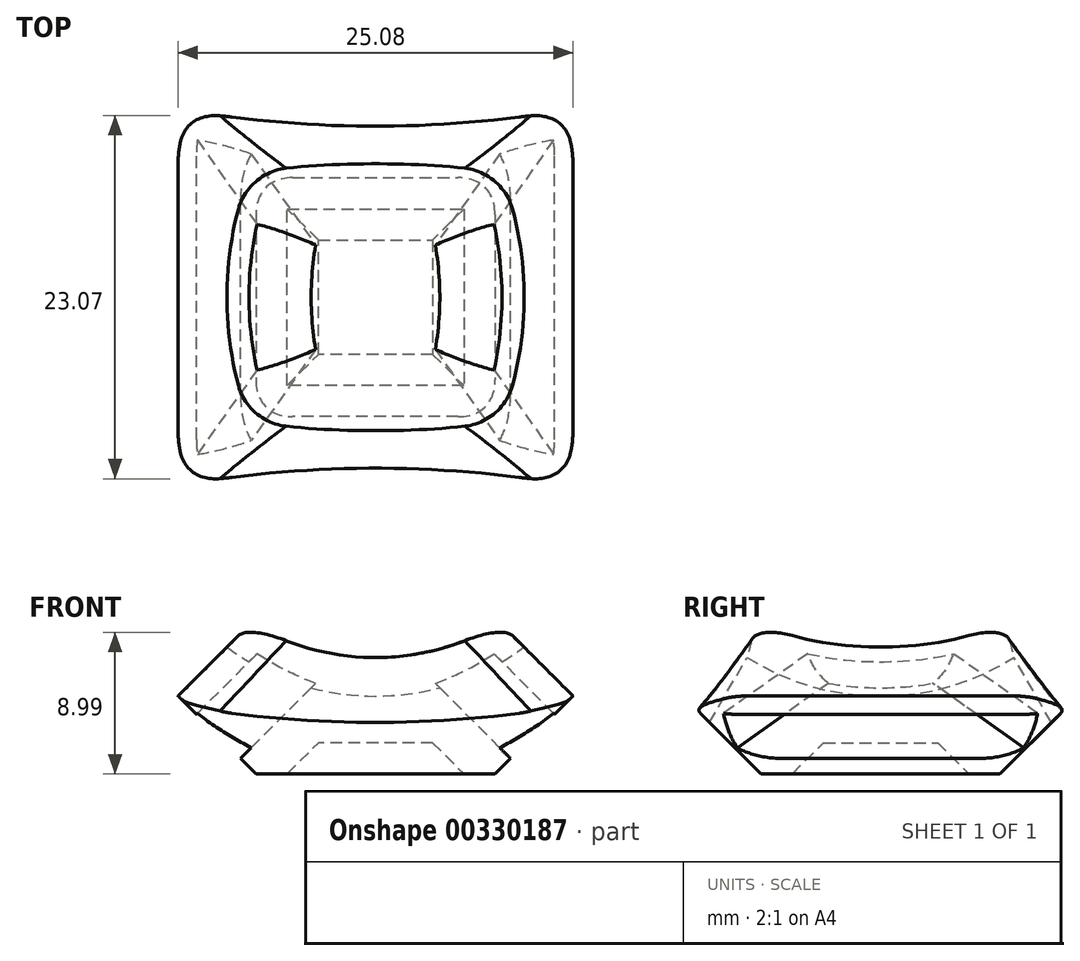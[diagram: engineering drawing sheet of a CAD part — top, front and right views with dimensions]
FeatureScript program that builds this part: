
annotation { "Feature Type Name" : "Feature", "Feature Type Description" : "" }
export const myFeature = defineFeature(function(context is Context, id is Id, definition is map)
    precondition{}
    {
        {
            var Q0;
            Q0=qCreatedBy(makeId("Top.planeOp"),FACE);
            var sketch = newSketch(context, id + "F0", { "sketchPlane" : qUnion([Q0])});
            skLineSegment(sketch, "E0.bottom", {"start": v(-12.43, 22.7) * mm, "end": v(7.57, 22.7) * mm});
            skLineSegment(sketch, "E0.top", {"start": v(-12.43, -17.3) * mm, "end": v(7.57, -17.3) * mm});
            skLineSegment(sketch, "E0.left", {"start": v(-12.43, 22.7) * mm, "end": v(-12.43, -17.3) * mm});
            skLineSegment(sketch, "E0.right", {"start": v(7.57, 22.7) * mm, "end": v(7.57, -17.3) * mm});
            skSolve(sketch);
        }
        {
            var Q0;
            Q0=qSketchRegion(id+"F0",true);
            extrude(context, id + "F1", {"entities" : qUnion([Q0]), "depth" : 20 * mm});
        }
        {
            var Q0;
            Q0=makeQuery(id+"F1.opExtrude","CAP_EDGE",EDGE,{"disambiguationData":[OSD([sQuery(id+"F0.wireOp",EDGE,"E0.right")])],"isStart":false});
            var Q1;
            Q1=makeQuery(id+"F1.opExtrude","CAP_EDGE",EDGE,{"disambiguationData":[OSD([sQuery(id+"F0.wireOp",EDGE,"E0.top")])],"isStart":false});
            var Q2;
            Q2=makeQuery(id+"F1.opExtrude","CAP_EDGE",EDGE,{"disambiguationData":[OSD([sQuery(id+"F0.wireOp",EDGE,"E0.bottom")])],"isStart":false});
            chamfer(context, id + "F2", {"entities" : qUnion([Q0, Q1, Q2]), "width" : 20 * mm, "tangentPropagation" : true});
        }
        {
            var Q0;
            Q0=makeQuery(id+"F1.opExtrude","CAP_FACE",FACE,{"disambiguationData":[OSD([sQuery(id+"F0.wireOp",EDGE,"E0.bottom"),sQuery(id+"F0.wireOp",EDGE,"E0.top"),sQuery(id+"F0.wireOp",EDGE,"E0.left"),sQuery(id+"F0.wireOp",EDGE,"E0.right")])],"isStart":true});
            extrude(context, id + "F3", {"entities" : qUnion([Q0]), "operationType" : NewBodyOperationType.ADD, "depth" : 6.5 * mm});
        }
        {
            var Q0;
            {var subQ0=sQuery(id+"F0.wireOp",EDGE,"E0.right");var subQ1=sQuery(id+"F0.wireOp",EDGE,"E0.left");var subQ2=sQuery(id+"F0.wireOp",EDGE,"E0.top");var subQ3=sQuery(id+"F0.wireOp",EDGE,"E0.bottom");Q0=makeQuery(id+"F3.opExtrude","CAP_EDGE",EDGE,{"disambiguationData":[OSD([subQ3,subQ2,subQ1,subQ0]),TDD([makeQuery(id+"F2.opChamfer","BLEND_EDGE",EDGE,{"blendedFrom":[makeQuery(id+"F1.opExtrude","CAP_EDGE",EDGE,{"disambiguationData":[OSD([subQ0])],"isStart":false}),makeQuery(id+"F1.opExtrude","CAP_FACE",FACE,{"disambiguationData":[OSD([subQ3,subQ2,subQ1,subQ0])],"isStart":true})],"blendedInto":[makeQuery(id+"F1.opExtrude","CAP_FACE",FACE,{"disambiguationData":[OSD([subQ3,subQ2,subQ1,subQ0])],"isStart":true})]})])],"isStart":false});}
            var Q1;
            {var subQ0=sQuery(id+"F0.wireOp",EDGE,"E0.right");var subQ1=sQuery(id+"F0.wireOp",EDGE,"E0.left");var subQ2=sQuery(id+"F0.wireOp",EDGE,"E0.top");var subQ3=sQuery(id+"F0.wireOp",EDGE,"E0.bottom");Q1=makeQuery(id+"F3.opExtrude","CAP_EDGE",EDGE,{"disambiguationData":[OSD([subQ3,subQ2,subQ1,subQ0]),TDD([makeQuery(id+"F2.opChamfer","BLEND_EDGE",EDGE,{"blendedFrom":[makeQuery(id+"F1.opExtrude","CAP_EDGE",EDGE,{"disambiguationData":[OSD([subQ3])],"isStart":false}),makeQuery(id+"F1.opExtrude","CAP_FACE",FACE,{"disambiguationData":[OSD([subQ3,subQ2,subQ1,subQ0])],"isStart":true})],"blendedInto":[makeQuery(id+"F1.opExtrude","CAP_FACE",FACE,{"disambiguationData":[OSD([subQ3,subQ2,subQ1,subQ0])],"isStart":true})]})])],"isStart":false});}
            var Q2;
            {var subQ0=sQuery(id+"F0.wireOp",EDGE,"E0.right");var subQ1=sQuery(id+"F0.wireOp",EDGE,"E0.left");var subQ2=sQuery(id+"F0.wireOp",EDGE,"E0.top");var subQ3=sQuery(id+"F0.wireOp",EDGE,"E0.bottom");Q2=makeQuery(id+"F3.opExtrude","CAP_EDGE",EDGE,{"disambiguationData":[OSD([subQ3,subQ2,subQ1,subQ0]),TDD([makeQuery(id+"F2.opChamfer","BLEND_EDGE",EDGE,{"blendedFrom":[makeQuery(id+"F1.opExtrude","CAP_EDGE",EDGE,{"disambiguationData":[OSD([subQ2])],"isStart":false}),makeQuery(id+"F1.opExtrude","CAP_FACE",FACE,{"disambiguationData":[OSD([subQ3,subQ2,subQ1,subQ0])],"isStart":true})],"blendedInto":[makeQuery(id+"F1.opExtrude","CAP_FACE",FACE,{"disambiguationData":[OSD([subQ3,subQ2,subQ1,subQ0])],"isStart":true})]})])],"isStart":false});}
            chamfer(context, id + "F4", {"entities" : qUnion([Q0, Q1, Q2]), "chamferType" : ChamferType.OFFSET_ANGLE, "width" : 8.5 * mm, "oppositeDirection" : false, "angle" : 45 * degree, "tangentPropagation" : true});
        }
        {
            var Q0;
            Q0=makeQuery(id+"F2.opChamfer","BLEND_FACE",FACE,{"disambiguationData":[OSD([sQuery(id+"F0.wireOp",EDGE,"E0.right")])]});
            cPlane(context, id + "F5", {"entities" : qUnion([Q0]), "cplaneType" : CPlaneType.OFFSET, "offset" : 5.5 * mm, "oppositeDirection" : true, "width" : 150 * mm, "height" : 150 * mm});
        }
        {
            var Q0;
            Q0=qCreatedBy(id+"F5.planeOp",FACE);
            var sketch = newSketch(context, id + "F6", { "sketchPlane" : qUnion([Q0])});
            skLineSegment(sketch, "E1", {"start": v(2.7, 11.3) * mm, "end": v(-12.55, -3.94) * mm});
            skLineSegment(sketch, "E2", {"start": v(-12.55, -3.94) * mm, "end": v(17.95, -3.94) * mm});
            skLineSegment(sketch, "E3", {"start": v(17.95, -3.94) * mm, "end": v(2.7, 11.3) * mm});
            skSolve(sketch);
        }
        {
            var Q0;
            Q0=qSketchRegion(id+"F6",true);
            extrude(context, id + "F7", {"entities" : qUnion([Q0]), "operationType" : NewBodyOperationType.REMOVE, "oppositeDirection" : true, "depth" : 6 * mm, "symmetric" : true});
        }
        {
            var Q0;
            Q0=makeQuery(id+"F1.opExtrude","SWEPT_BODY",BODY,{"disambiguationData":[OSD([sQuery(id+"F0.wireOp",EDGE,"E0.bottom"),sQuery(id+"F0.wireOp",EDGE,"E0.top"),sQuery(id+"F0.wireOp",EDGE,"E0.left"),sQuery(id+"F0.wireOp",EDGE,"E0.right")])]});
            var Q1;
            {var subQ0=sQuery(id+"F0.wireOp",EDGE,"E0.left");Q1=makeQuery(id+"F3.boolean.opBoolean","MERGE",FACE,{"derivedFrom":[makeQuery(id+"F1.opExtrude","SWEPT_FACE",FACE,{"disambiguationData":[OSD([subQ0])]}),makeQuery(id+"F3.opExtrude","SWEPT_FACE",FACE,{"disambiguationData":[OSD([subQ0])]})]});}
            mirror(context, id + "F8", {"operationType" : NewBodyOperationType.ADD, "entities" : qUnion([Q0]), "mirrorPlane" : qUnion([Q1])});
        }
        {
            var Q0;
            Q0=qCreatedBy(makeId("Top.planeOp"),FACE);
            cPlane(context, id + "F9", {"entities" : qUnion([Q0]), "cplaneType" : CPlaneType.OFFSET, "offset" : 25 * mm, "width" : 150 * mm, "height" : 150 * mm});
        }
        {
            var Q0;
            Q0=qCreatedBy(id+"F9.planeOp",FACE);
            var sketch = newSketch(context, id + "F10", { "sketchPlane" : qUnion([Q0])});
            skArc(sketch, "E4", {"start": v(-12.43, 26.72) * mm, "mid": v(-36.44, 2.7) * mm, "end": v(-12.43, -21.32) * mm});
            skLineSegment(sketch, "E5", {"start": v(-12.43, 40.8) * mm, "end": v(-12.43, -65.38) * mm, "construction": true});
            skLineSegment(sketch, "E6", {"start": v(-12.43, 26.72) * mm, "end": v(-12.43, -21.32) * mm});
            skSolve(sketch);
        }
        {
            var Q0;
            Q0=qCreatedBy(id+"F9.planeOp",FACE);
            cPlane(context, id + "F11", {"entities" : qUnion([Q0]), "cplaneType" : CPlaneType.OFFSET, "offset" : 41.1 * mm, "oppositeDirection" : true, "width" : 150 * mm, "height" : 150 * mm});
        }
        {
            var Q0;
            Q0=qSketchRegion(id+"F10",true);
            var Q1;
            Q1=sQuery(id+"F10.wireOp",EDGE,"E5");
            revolve(context, id + "F12", {"operationType" : NewBodyOperationType.REMOVE, "entities" : qUnion([Q0]), "axis" : qUnion([Q1]), "revolveType" : RevolveType.FULL, "oppositeDirection" : true});
        }
        {
            var Q0;
            Q0=qCreatedBy(id+"F11.planeOp",FACE);
            var sketch = newSketch(context, id + "F13", { "sketchPlane" : qUnion([Q0])});
            skCircle(sketch, "E7", {"center": v(-12.43, 87.55) * mm, "radius": 60 * mm});
            skCircle(sketch, "E8", {"center": v(-12.43, -82.15) * mm, "radius": 60 * mm});
            skLineSegment(sketch, "E9", {"start": v(-12.43, 87.55) * mm, "end": v(-12.43, -82.15) * mm, "construction": true});
            skSolve(sketch);
        }
        {
            var Q0;
            Q0=makeQuery(id+"F13.imprint","IMPRINT",FACE,{"disambiguationData":[TD([[makeQuery(id+"F13.imprint","IMPRINT",EDGE,{"derivedFrom":sQuery(id+"F13.wireOp",EDGE,"E7")}),1.0]])]});
            var Q1;
            Q1=makeQuery(id+"F13.imprint","IMPRINT",FACE,{"disambiguationData":[TD([[makeQuery(id+"F13.imprint","IMPRINT",EDGE,{"derivedFrom":sQuery(id+"F13.wireOp",EDGE,"E8")}),1.0]])]});
            extrude(context, id + "F14", {"entities" : qUnion([Q0, Q1]), "operationType" : NewBodyOperationType.REMOVE, "depth" : 33.1 * mm, "hasDraft" : true, "draftAngle" : 30 * degree});
        }
        {
            var Q0;
            {var subQ0=makeQuery(id+"F3.opExtrude","CAP_FACE",FACE,{"disambiguationData":[OSD([sQuery(id+"F0.wireOp",EDGE,"E0.bottom"),sQuery(id+"F0.wireOp",EDGE,"E0.top"),sQuery(id+"F0.wireOp",EDGE,"E0.left"),sQuery(id+"F0.wireOp",EDGE,"E0.right")])],"isStart":false});Q0=makeQuery(id+"F8.boolean.opBoolean","MERGE",FACE,{"derivedFrom":[subQ0,makeQuery(id+"F8.opPattern","COPY",FACE,{"derivedFrom":subQ0,"instanceName":"1"})]});}
            var sketch = newSketch(context, id + "F15", { "sketchPlane" : qUnion([Q0])});
            skLineSegment(sketch, "E10.bottom", {"start": v(-20.93, 5.8) * mm, "end": v(-3.93, 5.8) * mm});
            skLineSegment(sketch, "E10.top", {"start": v(-20.93, -11.2) * mm, "end": v(-3.93, -11.2) * mm});
            skLineSegment(sketch, "E10.left", {"start": v(-20.93, 5.8) * mm, "end": v(-20.93, -11.2) * mm});
            skLineSegment(sketch, "E10.right", {"start": v(-3.93, 5.8) * mm, "end": v(-3.93, -11.2) * mm});
            skPoint(sketch, "E10.middle", {"position": v(-12.43, -2.7) * mm});
            skPoint(sketch, "E10.middle.positionSnap0", {"position": v(-23.93, -2.7) * mm});
            skPoint(sketch, "E10.middle.positionSnap1", {"position": v(-12.43, 8.8) * mm});
            skPoint(sketch, "E10.centerSnap0", {"position": v(-23.93, -2.7) * mm});
            skPoint(sketch, "E10.centerSnap1", {"position": v(-12.43, 8.8) * mm});
            skSolve(sketch);
        }
        {
            var Q0;
            Q0 = qSketchRegion(id + "F15", true);
            extrude(context, id + "F16", {"entities" : qUnion([Q0]), "operationType" : NewBodyOperationType.REMOVE, "oppositeDirection" : true, "depth" : 3 * mm, "hasDraft" : true, "draftAngle" : 45 * degree, "draftPullDirection" : true});
        }
        {
            var Q0;
            Q0=makeQuery(id+"F14.boolean.opBoolean","INTERSECT",EDGE,{"derivedFrom":[makeQuery(id+"F2.opChamfer","BLEND_FACE",FACE,{"disambiguationData":[OSD([sQuery(id+"F0.wireOp",EDGE,"E0.right")])]}),makeQuery(id+"F14.opExtrude","SWEPT_FACE",FACE,{"disambiguationData":[OSD([sQuery(id+"F13.wireOp",EDGE,"E7")])]})]});
            var Q1;
            Q1=makeQuery(id+"F14.boolean.opBoolean","INTERSECT",EDGE,{"derivedFrom":[makeQuery(id+"F2.opChamfer","BLEND_FACE",FACE,{"disambiguationData":[OSD([sQuery(id+"F0.wireOp",EDGE,"E0.right")])]}),makeQuery(id+"F14.opExtrude","SWEPT_FACE",FACE,{"disambiguationData":[OSD([sQuery(id+"F13.wireOp",EDGE,"E8")])]})]});
            var Q2;
            Q2=makeQuery(id+"F14.boolean.opBoolean","INTERSECT",EDGE,{"derivedFrom":[makeQuery(id+"F8.opPattern","COPY",FACE,{"derivedFrom":makeQuery(id+"F2.opChamfer","BLEND_FACE",FACE,{"disambiguationData":[OSD([sQuery(id+"F0.wireOp",EDGE,"E0.right")])]}),"instanceName":"1"}),makeQuery(id+"F14.opExtrude","SWEPT_FACE",FACE,{"disambiguationData":[OSD([sQuery(id+"F13.wireOp",EDGE,"E8")])]})]});
            var Q3;
            Q3=makeQuery(id+"F14.boolean.opBoolean","INTERSECT",EDGE,{"derivedFrom":[makeQuery(id+"F8.opPattern","COPY",FACE,{"derivedFrom":makeQuery(id+"F2.opChamfer","BLEND_FACE",FACE,{"disambiguationData":[OSD([sQuery(id+"F0.wireOp",EDGE,"E0.right")])]}),"instanceName":"1"}),makeQuery(id+"F14.opExtrude","SWEPT_FACE",FACE,{"disambiguationData":[OSD([sQuery(id+"F13.wireOp",EDGE,"E7")])]})]});
            fillet(context, id + "F17", {"entities" : qUnion([Q0, Q1, Q2, Q3]), "radius" : 5 * mm, "tangentPropagation" : true, "allowEdgeOverflow" : false});
        }
        {
            var Q0;
            {var subQ0=sQuery(id+"F0.wireOp",EDGE,"E0.right");var subQ1=sQuery(id+"F0.wireOp",EDGE,"E0.left");var subQ2=sQuery(id+"F0.wireOp",EDGE,"E0.top");var subQ3=sQuery(id+"F0.wireOp",EDGE,"E0.bottom");var subQ4=makeQuery(id+"F1.opExtrude","CAP_FACE",FACE,{"disambiguationData":[OSD([subQ3,subQ2,subQ1,subQ0])],"isStart":true});var subQ5=makeQuery(id+"F3.opExtrude","CAP_EDGE",EDGE,{"disambiguationData":[OSD([subQ3,subQ2,subQ1,subQ0]),TDD([makeQuery(id+"F2.opChamfer","BLEND_EDGE",EDGE,{"blendedFrom":[makeQuery(id+"F1.opExtrude","CAP_EDGE",EDGE,{"disambiguationData":[OSD([subQ0])],"isStart":false}),subQ4],"blendedInto":[subQ4]})])],"isStart":false});var subQ6=makeQuery(id+"F3.opExtrude","CAP_EDGE",EDGE,{"disambiguationData":[OSD([subQ3,subQ2,subQ1,subQ0]),TDD([makeQuery(id+"F2.opChamfer","BLEND_EDGE",EDGE,{"blendedFrom":[makeQuery(id+"F1.opExtrude","CAP_EDGE",EDGE,{"disambiguationData":[OSD([subQ2])],"isStart":false}),subQ4],"blendedInto":[subQ4]})])],"isStart":false});Q0=makeQuery(id+"F7.boolean.opBoolean","SPLIT",EDGE,{"disambiguationData":[TD([makeQuery(id+"F2.opChamfer","BLEND_FACE",FACE,{"disambiguationData":[OSD([subQ2])]})])],"derivedFrom":makeQuery(id+"F4.opChamfer","BLEND_EDGE",EDGE,{"blendedFrom":[subQ6,subQ5],"blendedInto":[]})});}
            var Q1;
            {var subQ0=sQuery(id+"F0.wireOp",EDGE,"E0.right");var subQ1=sQuery(id+"F0.wireOp",EDGE,"E0.left");var subQ2=sQuery(id+"F0.wireOp",EDGE,"E0.top");var subQ3=sQuery(id+"F0.wireOp",EDGE,"E0.bottom");var subQ4=makeQuery(id+"F1.opExtrude","CAP_FACE",FACE,{"disambiguationData":[OSD([subQ3,subQ2,subQ1,subQ0])],"isStart":true});var subQ5=makeQuery(id+"F3.opExtrude","CAP_EDGE",EDGE,{"disambiguationData":[OSD([subQ3,subQ2,subQ1,subQ0]),TDD([makeQuery(id+"F2.opChamfer","BLEND_EDGE",EDGE,{"blendedFrom":[makeQuery(id+"F1.opExtrude","CAP_EDGE",EDGE,{"disambiguationData":[OSD([subQ0])],"isStart":false}),subQ4],"blendedInto":[subQ4]})])],"isStart":false});var subQ6=makeQuery(id+"F3.opExtrude","CAP_EDGE",EDGE,{"disambiguationData":[OSD([subQ3,subQ2,subQ1,subQ0]),TDD([makeQuery(id+"F2.opChamfer","BLEND_EDGE",EDGE,{"blendedFrom":[makeQuery(id+"F1.opExtrude","CAP_EDGE",EDGE,{"disambiguationData":[OSD([subQ2])],"isStart":false}),subQ4],"blendedInto":[subQ4]})])],"isStart":false});Q1=makeQuery(id+"F8.opPattern","COPY",EDGE,{"derivedFrom":makeQuery(id+"F7.boolean.opBoolean","SPLIT",EDGE,{"disambiguationData":[TD([makeQuery(id+"F2.opChamfer","BLEND_FACE",FACE,{"disambiguationData":[OSD([subQ2])]})])],"derivedFrom":makeQuery(id+"F4.opChamfer","BLEND_EDGE",EDGE,{"blendedFrom":[subQ6,subQ5],"blendedInto":[]})}),"instanceName":"1"});}
            var Q2;
            {var subQ0=sQuery(id+"F0.wireOp",EDGE,"E0.right");var subQ1=sQuery(id+"F0.wireOp",EDGE,"E0.left");var subQ2=sQuery(id+"F0.wireOp",EDGE,"E0.top");var subQ3=sQuery(id+"F0.wireOp",EDGE,"E0.bottom");var subQ4=makeQuery(id+"F1.opExtrude","CAP_FACE",FACE,{"disambiguationData":[OSD([subQ3,subQ2,subQ1,subQ0])],"isStart":true});var subQ5=makeQuery(id+"F3.opExtrude","CAP_EDGE",EDGE,{"disambiguationData":[OSD([subQ3,subQ2,subQ1,subQ0]),TDD([makeQuery(id+"F2.opChamfer","BLEND_EDGE",EDGE,{"blendedFrom":[makeQuery(id+"F1.opExtrude","CAP_EDGE",EDGE,{"disambiguationData":[OSD([subQ3])],"isStart":false}),subQ4],"blendedInto":[subQ4]})])],"isStart":false});var subQ6=makeQuery(id+"F3.opExtrude","CAP_EDGE",EDGE,{"disambiguationData":[OSD([subQ3,subQ2,subQ1,subQ0]),TDD([makeQuery(id+"F2.opChamfer","BLEND_EDGE",EDGE,{"blendedFrom":[makeQuery(id+"F1.opExtrude","CAP_EDGE",EDGE,{"disambiguationData":[OSD([subQ0])],"isStart":false}),subQ4],"blendedInto":[subQ4]})])],"isStart":false});Q2=makeQuery(id+"F8.opPattern","COPY",EDGE,{"derivedFrom":makeQuery(id+"F7.boolean.opBoolean","SPLIT",EDGE,{"disambiguationData":[TD([makeQuery(id+"F2.opChamfer","BLEND_FACE",FACE,{"disambiguationData":[OSD([subQ3])]})])],"derivedFrom":makeQuery(id+"F4.opChamfer","BLEND_EDGE",EDGE,{"blendedFrom":[subQ5,subQ6],"blendedInto":[]})}),"instanceName":"1"});}
            var Q3;
            {var subQ0=sQuery(id+"F0.wireOp",EDGE,"E0.right");var subQ1=sQuery(id+"F0.wireOp",EDGE,"E0.left");var subQ2=sQuery(id+"F0.wireOp",EDGE,"E0.top");var subQ3=sQuery(id+"F0.wireOp",EDGE,"E0.bottom");var subQ4=makeQuery(id+"F1.opExtrude","CAP_FACE",FACE,{"disambiguationData":[OSD([subQ3,subQ2,subQ1,subQ0])],"isStart":true});var subQ5=makeQuery(id+"F3.opExtrude","CAP_EDGE",EDGE,{"disambiguationData":[OSD([subQ3,subQ2,subQ1,subQ0]),TDD([makeQuery(id+"F2.opChamfer","BLEND_EDGE",EDGE,{"blendedFrom":[makeQuery(id+"F1.opExtrude","CAP_EDGE",EDGE,{"disambiguationData":[OSD([subQ3])],"isStart":false}),subQ4],"blendedInto":[subQ4]})])],"isStart":false});var subQ6=makeQuery(id+"F3.opExtrude","CAP_EDGE",EDGE,{"disambiguationData":[OSD([subQ3,subQ2,subQ1,subQ0]),TDD([makeQuery(id+"F2.opChamfer","BLEND_EDGE",EDGE,{"blendedFrom":[makeQuery(id+"F1.opExtrude","CAP_EDGE",EDGE,{"disambiguationData":[OSD([subQ0])],"isStart":false}),subQ4],"blendedInto":[subQ4]})])],"isStart":false});Q3=makeQuery(id+"F7.boolean.opBoolean","SPLIT",EDGE,{"disambiguationData":[TD([makeQuery(id+"F2.opChamfer","BLEND_FACE",FACE,{"disambiguationData":[OSD([subQ3])]})])],"derivedFrom":makeQuery(id+"F4.opChamfer","BLEND_EDGE",EDGE,{"blendedFrom":[subQ5,subQ6],"blendedInto":[]})});}
            fillet(context, id + "F18", {"entities" : qUnion([Q0, Q1, Q2, Q3]), "radius" : 5 * mm, "tangentPropagation" : true, "allowEdgeOverflow" : false});
        }
        {
            var Q0;
            Q0=makeQuery(id+"F1.opExtrude","SWEPT_BODY",BODY,{"disambiguationData":[OSD([sQuery(id+"F0.wireOp",EDGE,"E0.bottom"),sQuery(id+"F0.wireOp",EDGE,"E0.top"),sQuery(id+"F0.wireOp",EDGE,"E0.left"),sQuery(id+"F0.wireOp",EDGE,"E0.right")])]});
            var Q1;
            {var subQ0=sQuery(id+"F6.wireOp",EDGE,"E3");Q1=makeQuery(id+"F12.boolean.opBoolean","INTERSECT",VERTEX,{"derivedFrom":[makeQuery(id+"F8.opPattern","COPY",FACE,{"derivedFrom":makeQuery(id+"F7.boolean.opBoolean","COPY",FACE,{"derivedFrom":makeQuery(id+"F7.opExtrude","CAP_FACE",FACE,{"disambiguationData":[OSD([sQuery(id+"F6.wireOp",EDGE,"E1"),sQuery(id+"F6.wireOp",EDGE,"E2"),subQ0])],"isStart":false})}),"instanceName":"1"}),makeQuery(id+"F8.opPattern","COPY",FACE,{"derivedFrom":makeQuery(id+"F7.boolean.opBoolean","COPY",FACE,{"derivedFrom":makeQuery(id+"F7.opExtrude","SWEPT_FACE",FACE,{"disambiguationData":[OSD([subQ0])]})}),"instanceName":"1"}),makeQuery(id+"F12.opRevolve","SWEPT_FACE",FACE,{"disambiguationData":[OSD([sQuery(id+"F10.wireOp",EDGE,"E4")])]})]});}
            transform(context, id + "F19", {"entities" : qUnion([Q0]), "transformType" : TransformType.SCALE_UNIFORMLY, "scale" : 0.66, "scalePoint" : qUnion([Q1]), "makeCopy" : false});
        }
    });
